# Revit family: Vitra-Plural-62570
name_source: partatom
category: Furniture Systems
revit_build: Autodesk Revit 2017 (Build: 20160225_1515(x64)
units: mm (PartAtom-declared; Revit-internal decimal feet)

## family parameters
Cut with Voids When Loaded = No
Host = Face
OmniClass Number = 23.40.00.00
OmniClass Title = Equipment and Furnishings
Part Type = Normal
Room Calculation Point = No
Round Connector Dimension = Use Diameter
Shared = Yes

## types (5) — shared parameters
BIMobject category = Bathroom compound units
Construction Type = Face Mounted
Default Elevation = 710 mm
Depth = 610 mm  [stored 2.00131 ft]
Description = Plural Washbasin Unit
Design country = Turkey
Height = 710 mm
IFC Classification = Furniture
Manufacturer = Vitra
Manufacturer name = Vitra
Masterformat 2014 Code = 13 42 13
Masterformat 2014 Description = Bathroom Unit Modules
NBS Referans Code = 35-75-08
NBS Referans Description = Bathroom Cabinets
Nominal height = 0.000
Nominal width = 0.000
OmniClass Code = 23-31 25 13
OmniClass Description = Bathroom Cabinets
Product certification = https://vitraglobal.com
Product data url = https://www.vitra.com.tr
Product family = Plural
Product group = Washbasin Unit
Secondary Material = Vitra-DarkOlive
Thrid Material = Vitra-AmericanValnut
UNSPSC Code = 301815
UNSPSC Description = Bathroom Cabinets
URL = https://vitraglobal.com
Uniclass 1.4 Code = L8241
Uniclass 1.4 Description = Bathroom Cabinets
Uniclass 2.0 Code = PR-35-75-08
Uniclass 2.0 Description = Bathroom Cabinets
Uniclass 2015 Code = Pr_40_20_93
Uniclass 2015 Name = Wash basins, sinks and troughs
Uniformat II Code = E20
Uniformat II Description = FURNISHINGS
Warranty Period (Year) = 2
Weight Net (kg) = 33,200
Width = 1000 mm  [stored 3.28084 ft]
Youtube = https://www.youtube.com

## per-type parameters (varying)
| type | Article No. (default) | Color | Model | Primary Material | Product SKU |
| WashbasinUnit-Vitra-Plural-CeramicCountertop(White)_62570 | 62570 | White | 62570 | Vitra-White | 62570 |
| WashbasinUnit-Vitra-Plural-CeramicCountertop(MatteWhite)_62571 | 62571 | Matte White | 62571 | Vitra-MattWhite | 62571 |
| WashbasinUnit-Vitra-Plural-CeramicCountertop(MatteBlack)_62572 | 62572 | Matte Black | 62572 | Vitra-DarkOlive | 62572 |
| WashbasinUnit-Vitra-Plural-CeramicCountertop(MatteBeige)_62573 | 62573 | Matte Beige | 62573 | Vitra-MatteBeige | 62573 |
| WashbasinUnit-Vitra-Plural-CeramicCountertop(MatteMink)_62574 | 62574 | Matte Mink | 62574 | Vitra-MatteMink | 62574 |

note: [stored X ft] marks values corroborated as IEEE doubles in the binary element streams (Revit-internal decimal feet)

## geometry (parser evidence)
native form markers: Sweep x3
no freeform markers — native parametric forms only
